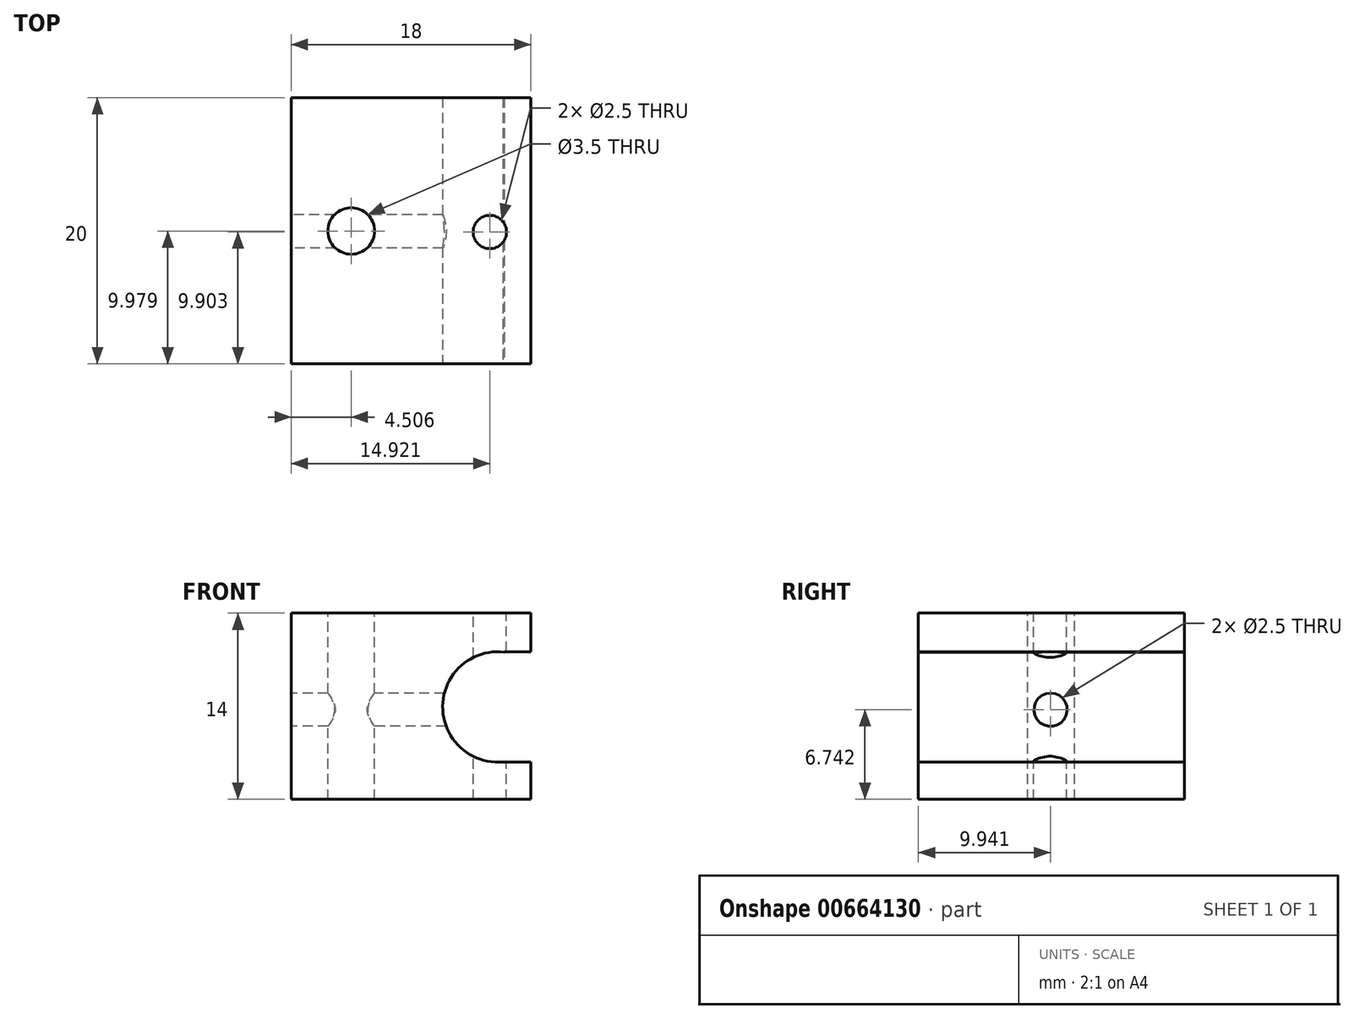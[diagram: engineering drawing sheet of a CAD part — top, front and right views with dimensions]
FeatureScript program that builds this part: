
annotation { "Feature Type Name" : "Feature", "Feature Type Description" : "" }
export const myFeature = defineFeature(function(context is Context, id is Id, definition is map)
    precondition{}
    {
        {
            var Q0;
            Q0=qCreatedBy(makeId("Front.planeOp"),FACE);
            var sketch = newSketch(context, id + "F0", { "sketchPlane" : qUnion([Q0])});
            skLineSegment(sketch, "E0.bottom", {"start": v(-4.95, 27.75) * mm, "end": v(13.05, 27.75) * mm});
            skLineSegment(sketch, "E0.top", {"start": v(-4.95, 13.75) * mm, "end": v(13.05, 13.75) * mm});
            skLineSegment(sketch, "E0.left", {"start": v(-4.95, 27.75) * mm, "end": v(-4.95, 13.75) * mm});
            skLineSegment(sketch, "E0.right", {"start": v(13.05, 27.75) * mm, "end": v(13.05, 13.75) * mm});
            skSolve(sketch);
        }
        {
            var Q0;
            Q0=makeQuery(id+"F0.imprint","IMPRINT",FACE,{"disambiguationData":[TD([[makeQuery(id+"F0.imprint","IMPRINT",EDGE,{"derivedFrom":sQuery(id+"F0.wireOp",EDGE,"E0.bottom")}),-1.0]])]});
            extrude(context, id + "F1", {"entities" : qUnion([Q0]), "depth" : 20 * mm, "offsetDistance" : 25 * mm});
        }
        {
            var Q0;
            Q0=makeQuery(id+"F1.opExtrude","CAP_FACE",FACE,{"disambiguationData":[OSD([sQuery(id+"F0.wireOp",EDGE,"E0.bottom"),sQuery(id+"F0.wireOp",EDGE,"E0.top"),sQuery(id+"F0.wireOp",EDGE,"E0.left"),sQuery(id+"F0.wireOp",EDGE,"E0.right")])],"isStart":false});
            var sketch = newSketch(context, id + "F2", { "sketchPlane" : qUnion([Q0])});
            skCircle(sketch, "E1", {"center": v(10.58, 20.7) * mm, "radius": 4.15 * mm});
            skLineSegment(sketch, "E2.top", {"start": v(11.05, 24.85) * mm, "end": v(13.05, 24.85) * mm});
            skLineSegment(sketch, "E2.left", {"start": v(11.05, 24.82) * mm, "end": v(11.05, 24.85) * mm});
            skLineSegment(sketch, "E2.right", {"start": v(13.05, 24.85) * mm, "end": v(13.05, 24.86) * mm});
            skLineSegment(sketch, "E3.left", {"start": v(10.94, 16.45) * mm, "end": v(10.94, 16.57) * mm});
            skLineSegment(sketch, "E3.right", {"start": v(13.05, 16.45) * mm, "end": v(13.05, 16.56) * mm});
            skLineSegment(sketch, "E4", {"start": v(13.05, 24.86) * mm, "end": v(13.05, 24.03) * mm});
            skLineSegment(sketch, "E5", {"start": v(10.94, 16.57) * mm, "end": v(13.05, 16.56) * mm});
            skLineSegment(sketch, "E6", {"start": v(13.05, 16.56) * mm, "end": v(13.05, 17.37) * mm});
            skSolve(sketch);
        }
        {
            var Q0;
            {var subQ0=sQuery(id+"F2.wireOp",EDGE,"E1");var subQ1=makeQuery(id+"F2.imprint","INTERSECT",VERTEX,{"derivedFrom":[subQ0,sQuery(id+"F2.wireOp",EDGE,"E2.left")]});Q0=makeQuery(id+"F2.imprint","IMPRINT",FACE,{"disambiguationData":[TD([[makeQuery(id+"F2.imprint","IMPRINT",EDGE,{"disambiguationData":[TD([[subQ1,1.0]])],"derivedFrom":subQ0}),1.0]])]});}
            var Q1;
            {var subQ0=sQuery(id+"F2.wireOp",EDGE,"E5");Q1=makeQuery(id+"F2.imprint","IMPRINT",FACE,{"disambiguationData":[TD([[makeQuery(id+"F2.imprint","IMPRINT",EDGE,{"derivedFrom":subQ0}),1.0]])]});}
            var Q2;
            {var subQ4=sQuery(id+"F2.wireOp",EDGE,"E2.top");Q2=makeQuery(id+"F2.imprint","IMPRINT",FACE,{"disambiguationData":[TD([[makeQuery(id+"F2.imprint","IMPRINT",EDGE,{"derivedFrom":subQ4}),-1.0]])]});}
            extrude(context, id + "F3", {"entities" : qUnion([Q0, Q1, Q2]), "operationType" : NewBodyOperationType.REMOVE, "oppositeDirection" : true, "depth" : 20 * mm, "offsetDistance" : 25 * mm});
        }
        {
            var Q0;
            Q0=makeQuery(id+"F1.opExtrude","SWEPT_FACE",FACE,{"disambiguationData":[OSD([sQuery(id+"F0.wireOp",EDGE,"E0.bottom")])]});
            var sketch = newSketch(context, id + "F4", { "sketchPlane" : qUnion([Q0])});
            skCircle(sketch, "E7", {"center": v(9.97, -10.1) * mm, "radius": 1.25 * mm});
            skCircle(sketch, "E8", {"center": v(-0.44, -10.02) * mm, "radius": 1.75 * mm});
            skSolve(sketch);
        }
        {
            var Q0;
            Q0=makeQuery(id+"F4.imprint","IMPRINT",FACE,{"disambiguationData":[TD([[makeQuery(id+"F4.imprint","IMPRINT",EDGE,{"derivedFrom":sQuery(id+"F4.wireOp",EDGE,"E7")}),1.0]])]});
            var Q1;
            Q1=makeQuery(id+"F4.imprint","IMPRINT",FACE,{"disambiguationData":[TD([[makeQuery(id+"F4.imprint","IMPRINT",EDGE,{"derivedFrom":sQuery(id+"F4.wireOp",EDGE,"E8")}),1.0]])]});
            extrude(context, id + "F5", {"entities" : qUnion([Q0, Q1]), "operationType" : NewBodyOperationType.REMOVE, "oppositeDirection" : true, "depth" : 25 * mm, "offsetDistance" : 25 * mm});
        }
        {
            var Q0;
            Q0=makeQuery(id+"F1.opExtrude","SWEPT_FACE",FACE,{"disambiguationData":[OSD([sQuery(id+"F0.wireOp",EDGE,"E0.left")])]});
            var sketch = newSketch(context, id + "F6", { "sketchPlane" : qUnion([Q0])});
            skCircle(sketch, "E9", {"center": v(10.06, 20.5) * mm, "radius": 1.25 * mm});
            skSolve(sketch);
        }
        {
            var Q0;
            Q0=makeQuery(id+"F6.imprint","IMPRINT",FACE,{"disambiguationData":[TD([[makeQuery(id+"F6.imprint","IMPRINT",EDGE,{"derivedFrom":sQuery(id+"F6.wireOp",EDGE,"E9")}),1.0]])]});
            extrude(context, id + "F7", {"entities" : qUnion([Q0]), "operationType" : NewBodyOperationType.REMOVE, "oppositeDirection" : true, "depth" : 25 * mm, "offsetDistance" : 25 * mm});
        }
    });
